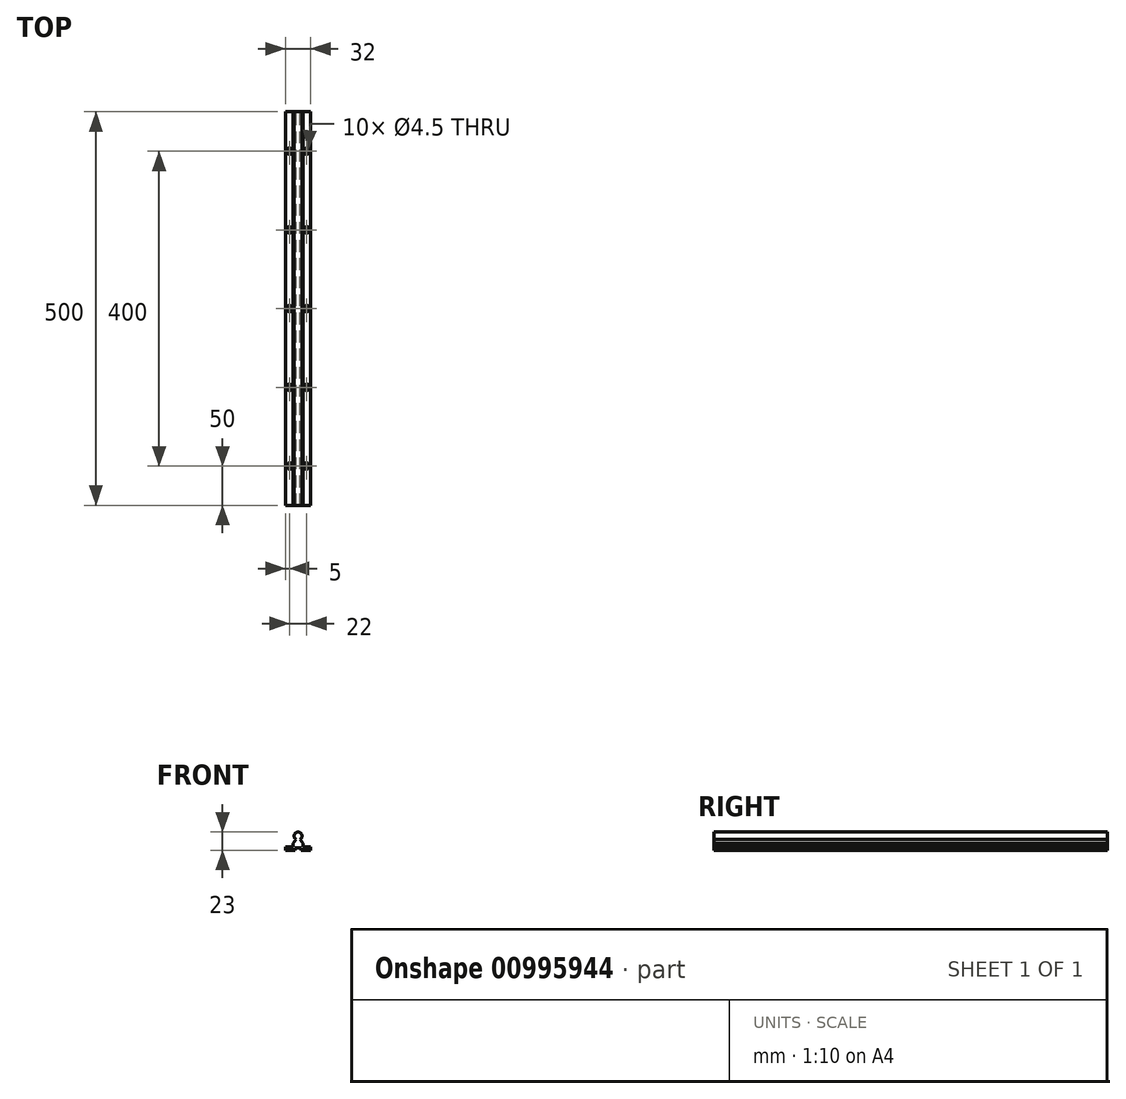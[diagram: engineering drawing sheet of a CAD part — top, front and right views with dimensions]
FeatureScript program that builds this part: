
annotation { "Feature Type Name" : "Feature", "Feature Type Description" : "" }
export const myFeature = defineFeature(function(context is Context, id is Id, definition is map)
    precondition{}
    {
        {
            assignVariable(context, id + "F0", {"name" : "Len", "anyValue" : 500});
        }
        {
            var Q0;
            Q0=qCreatedBy(makeId("Front.planeOp"),FACE);
            var sketch = newSketch(context, id + "F1", { "sketchPlane" : qUnion([Q0])});
            skLineSegment(sketch, "E0.bottom", {"start": v(-16, 0) * mm, "end": v(16, 0) * mm});
            skLineSegment(sketch, "E0.top", {"start": v(-16, 4) * mm, "end": v(16, 4) * mm});
            skLineSegment(sketch, "E0.left", {"start": v(-16, 0) * mm, "end": v(-16, 4) * mm});
            skLineSegment(sketch, "E0.right", {"start": v(16, 0) * mm, "end": v(16, 4) * mm});
            skLineSegment(sketch, "E1.bottom", {"start": v(-6.2, 0) * mm, "end": v(6.2, 0) * mm});
            skLineSegment(sketch, "E1.top", {"start": v(-6.2, 8.9) * mm, "end": v(6.2, 8.9) * mm});
            skLineSegment(sketch, "E1.left", {"start": v(-6.2, 0) * mm, "end": v(-6.2, 8.9) * mm});
            skLineSegment(sketch, "E1.right", {"start": v(6.2, 0) * mm, "end": v(6.2, 8.9) * mm});
            skLineSegment(sketch, "E2", {"start": v(0, 0) * mm, "end": v(0, 26.12) * mm, "construction": true});
            skCircle(sketch, "E3", {"center": v(0, 18) * mm, "radius": 5 * mm});
            skLineSegment(sketch, "E4", {"start": v(6.2, 8.9) * mm, "end": v(2.35, 13.59) * mm});
            skLineSegment(sketch, "E5.MirrorCS", {"start": v(-6.2, 8.9) * mm, "end": v(-2.35, 13.59) * mm});
            skLineSegment(sketch, "E6.bottom", {"start": v(4, 0) * mm, "end": v(-4, 0) * mm});
            skLineSegment(sketch, "E6.top", {"start": v(4, 3) * mm, "end": v(-4, 3) * mm});
            skLineSegment(sketch, "E6.left", {"start": v(4, 0) * mm, "end": v(4, 3) * mm});
            skLineSegment(sketch, "E6.right", {"start": v(-4, 0) * mm, "end": v(-4, 3) * mm});
            skSolve(sketch);
        }
        {
            var Q0;
            Q0=qCreatedBy(makeId("Front.planeOp"),FACE);
            cPlane(context, id + "F2", {"entities" : qUnion([Q0]), "cplaneType" : CPlaneType.OFFSET, "offset" : (getVariable(context, 'Len')) * mm, "width" : 150 * mm, "height" : 150 * mm});
        }
        {
            var Q0;
            {var subQ0=sQuery(id+"F1.wireOp",EDGE,"E0.right");Q0=makeQuery(id+"F1.imprint","IMPRINT",FACE,{"disambiguationData":[TD([[makeQuery(id+"F1.imprint","IMPRINT",EDGE,{"derivedFrom":subQ0}),1.0]])]});}
            var Q1;
            Q1=makeQuery(id+"F1.imprint","IMPRINT",FACE,{"disambiguationData":[TD([[makeQuery(id+"F1.imprint","IMPRINT",EDGE,{"derivedFrom":sQuery(id+"F1.wireOp",EDGE,"E6.top")}),-1.0]])]});
            var Q2;
            {var subQ5=sQuery(id+"F1.wireOp",EDGE,"E1.top");Q2=makeQuery(id+"F1.imprint","IMPRINT",FACE,{"disambiguationData":[TD([[makeQuery(id+"F1.imprint","IMPRINT",EDGE,{"derivedFrom":subQ5}),-1.0]])]});}
            var Q3;
            {var subQ0=sQuery(id+"F1.wireOp",EDGE,"E3");var subQ1=makeQuery(id+"F1.imprint","INTERSECT",VERTEX,{"derivedFrom":[subQ0,sQuery(id+"F1.wireOp",EDGE,"E4")]});Q3=makeQuery(id+"F1.imprint","IMPRINT",FACE,{"disambiguationData":[TD([[makeQuery(id+"F1.imprint","IMPRINT",EDGE,{"disambiguationData":[TD([[subQ1,1.0]])],"derivedFrom":subQ0}),1.0]])]});}
            var Q4;
            {var subQ0=sQuery(id+"F1.wireOp",EDGE,"E0.left");Q4=makeQuery(id+"F1.imprint","IMPRINT",FACE,{"disambiguationData":[TD([[makeQuery(id+"F1.imprint","IMPRINT",EDGE,{"derivedFrom":subQ0}),-1.0]])]});}
            var Q5;
            Q5=makeQuery(id+"F1.imprint","IMPRINT",FACE,{"disambiguationData":[TD([[makeQuery(id+"F1.imprint","IMPRINT",EDGE,{"derivedFrom":sQuery(id+"F1.wireOp",EDGE,"E1.top")}),1.0]])]});
            var Q6;
            Q6=qCreatedBy(id+"F2.planeOp",FACE);
            extrude(context, id + "F3", {"entities" : qUnion([Q0, Q1, Q2, Q3, Q4, Q5]), "endBound" : BoundingType.UP_TO_SURFACE, "depth" : 25 * mm, "endBoundEntityFace" : qUnion([Q6]), "offsetDistance" : 25 * mm});
        }
        {
            var Q0;
            {var subQ0=sQuery(id+"F1.wireOp",EDGE,"E0.top");Q0=makeQuery(id+"F3.opExtrude","SWEPT_FACE",FACE,{"disambiguationData":[OSD([subQ0]),TDD([makeQuery(id+"F1.imprint","IMPRINT",EDGE,{"disambiguationData":[TD([[makeQuery(id+"F1.imprint","INTERSECT",VERTEX,{"derivedFrom":[subQ0,sQuery(id+"F1.wireOp",EDGE,"E0.right")]}),1.0]])],"derivedFrom":subQ0})])]});}
            var sketch = newSketch(context, id + "F4", { "sketchPlane" : qUnion([Q0])});
            skPoint(sketch, "E7", {"position": v(-11, -50) * mm});
            skPoint(sketch, "E8.MirrorP", {"position": v(11, -50) * mm});
            skLineSegment(sketch, "E9", {"start": v(-16.92, -250) * mm, "end": v(16, -250) * mm, "construction": true});
            skPoint(sketch, "E9.startSnap0", {"position": v(16, -250) * mm});
            skPoint(sketch, "E10.0.1.0", {"position": v(-11, -150) * mm});
            skPoint(sketch, "E10.0.1.1", {"position": v(11, -150) * mm});
            skPoint(sketch, "E10.0.2.0", {"position": v(-11, -250) * mm});
            skPoint(sketch, "E10.0.2.1", {"position": v(11, -250) * mm});
            skPoint(sketch, "E10.0.3.0", {"position": v(-11, -350) * mm});
            skPoint(sketch, "E10.0.3.1", {"position": v(11, -350) * mm});
            skPoint(sketch, "E10.0.4.0", {"position": v(-11, -450) * mm});
            skPoint(sketch, "E10.0.4.1", {"position": v(11, -450) * mm});
            skLineSegment(sketch, "E10.direction1", {"start": v(-11, -50) * mm, "end": v(14, -50) * mm, "construction": true});
            skLineSegment(sketch, "E10.direction2", {"start": v(-11, -50) * mm, "end": v(-11, -150) * mm, "construction": true});
            skSolve(sketch);
        }
        {
            var Q0;
            Q0=sQuery(id+"F4.wireOp",VERTEX,"E8.MirrorP");
            var Q1;
            Q1=sQuery(id+"F4.wireOp",VERTEX,"E7");
            var Q2;
            Q2=sQuery(id+"F4.wireOp",VERTEX,"E10.0.1.0");
            var Q3;
            Q3=sQuery(id+"F4.wireOp",VERTEX,"E10.0.1.1");
            var Q4;
            Q4=sQuery(id+"F4.wireOp",VERTEX,"E10.0.2.1");
            var Q5;
            Q5=sQuery(id+"F4.wireOp",VERTEX,"E10.0.2.0");
            var Q6;
            Q6=sQuery(id+"F4.wireOp",VERTEX,"E10.0.3.1");
            var Q7;
            Q7=sQuery(id+"F4.wireOp",VERTEX,"E10.0.3.0");
            var Q8;
            Q8=sQuery(id+"F4.wireOp",VERTEX,"E10.0.4.1");
            var Q9;
            Q9=sQuery(id+"F4.wireOp",VERTEX,"E10.0.4.0");
            var Q10;
            Q10=makeQuery(id+"F3.opExtrude","SWEPT_BODY",BODY,{"disambiguationData":[OSD([sQuery(id+"F1.wireOp",EDGE,"E0.bottom"),sQuery(id+"F1.wireOp",EDGE,"E0.top"),sQuery(id+"F1.wireOp",EDGE,"E0.left"),sQuery(id+"F1.wireOp",EDGE,"E0.right"),sQuery(id+"F1.wireOp",EDGE,"E1.bottom"),sQuery(id+"F1.wireOp",EDGE,"E1.left"),sQuery(id+"F1.wireOp",EDGE,"E1.right"),sQuery(id+"F1.wireOp",EDGE,"E3"),sQuery(id+"F1.wireOp",EDGE,"E4"),sQuery(id+"F1.wireOp",EDGE,"E5.MirrorCS")])]});
            hole(context, id + "F5", {"style" : HoleStyle.C_SINK, "endStyle" : HoleEndStyle.THROUGH, "standardTappedOrClearance" : lookupTablePath({ "standard" : "ISO", "size" : "4.5", "type" : "Drilled" }), "standardBlindInLast" : lookupTablePath({ "standard" : "ISO", "size" : "4.5", "type" : "Drilled" }), "holeDiameter" : 4.5 * mm, "cSinkDiameter" : 8 * mm, "cSinkAngle" : 90 * degree, "majorDiameter" : 5 * mm, "isTappedThrough" : true, "tappedDepth" : 12 * mm, "tapClearance" : 3, "locations" : qUnion([Q0, Q1, Q2, Q3, Q4, Q5, Q6, Q7, Q8, Q9]), "scope" : qUnion([Q10])});
        }
        {
            var Q0;
            Q0=makeQuery(id+"F3.opExtrude","SWEPT_BODY",BODY,{"disambiguationData":[OSD([sQuery(id+"F1.wireOp",EDGE,"E0.bottom"),sQuery(id+"F1.wireOp",EDGE,"E0.top"),sQuery(id+"F1.wireOp",EDGE,"E0.left"),sQuery(id+"F1.wireOp",EDGE,"E0.right"),sQuery(id+"F1.wireOp",EDGE,"E1.bottom"),sQuery(id+"F1.wireOp",EDGE,"E1.left"),sQuery(id+"F1.wireOp",EDGE,"E1.right"),sQuery(id+"F1.wireOp",EDGE,"E3"),sQuery(id+"F1.wireOp",EDGE,"E4"),sQuery(id+"F1.wireOp",EDGE,"E5.MirrorCS"),sQuery(id+"F1.wireOp",EDGE,"E6.top"),sQuery(id+"F1.wireOp",EDGE,"E6.left"),sQuery(id+"F1.wireOp",EDGE,"E6.right")])]});
            transform(context, id + "F6", {"entities" : qUnion([Q0]), "transformType" : TransformType.TRANSLATION_3D, "dx" : 0 * mm, "dy" : 0 * mm, "dz" : 0 * mm, "makeCopy" : true});
        }
        {
            var Q0;
            Q0=makeQuery(id+"F6.opPattern","COPY",BODY,{"derivedFrom":makeQuery(id+"F3.opExtrude","SWEPT_BODY",BODY,{"disambiguationData":[OSD([sQuery(id+"F1.wireOp",EDGE,"E0.bottom"),sQuery(id+"F1.wireOp",EDGE,"E0.top"),sQuery(id+"F1.wireOp",EDGE,"E0.left"),sQuery(id+"F1.wireOp",EDGE,"E0.right"),sQuery(id+"F1.wireOp",EDGE,"E1.bottom"),sQuery(id+"F1.wireOp",EDGE,"E1.left"),sQuery(id+"F1.wireOp",EDGE,"E1.right"),sQuery(id+"F1.wireOp",EDGE,"E3"),sQuery(id+"F1.wireOp",EDGE,"E4"),sQuery(id+"F1.wireOp",EDGE,"E5.MirrorCS"),sQuery(id+"F1.wireOp",EDGE,"E6.top"),sQuery(id+"F1.wireOp",EDGE,"E6.left"),sQuery(id+"F1.wireOp",EDGE,"E6.right")])]}),"instanceName":"1"});
            deleteBodies(context, id + "F7", {"entities" : qUnion([Q0])});
        }
    });
